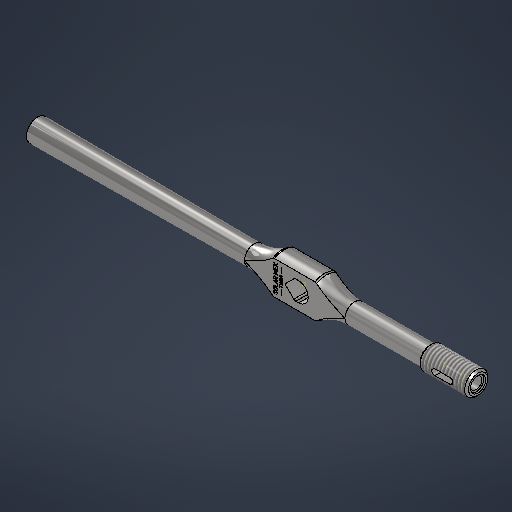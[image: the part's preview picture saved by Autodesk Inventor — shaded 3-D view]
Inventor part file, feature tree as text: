
AUTODESK INVENTOR PART (.ipt)
format: ipt  version: 2025.3 (Build 293356000, 356)  size: 490,496 bytes
history: native  units: mm
features: sketch x5, extrude x2, other x2, fillet x2, revolve x1, thread x1, plane x1, projected_geometry x1
ambient origin geometry x8: Origin, YZ Plane, XZ Plane, XY Plane, X Axis, Y Axis, Z Axis, Center Point
bodies: Solid1 (feature_tree)
feature tree (15):
  sketch  "Sketch1"  dims[d0=7.071068mm d3=2.071068mm]
  revolve  "Revolution1"  [1 undecoded]
  extrude  "Extrusion1"  Depth=52.0mm
  extrude  "Extrusion2"  Depth=1.5mm
  thread  "Thread1"  [1 undecoded]
  other  "Mark2"
  plane  "Work Plane1"
  fillet  "Fillet3"  Radius=6.0mm
  fillet  "Fillet4"  Radius=1.5mm
  sketch  "Sketch5"  dims[d24=1.0mm]
  other  "Work Axis1"
  sketch  "Sketch6"  dims[d25=12.0mm d26=1.0mm d27=1.0mm d28=90.0mm d29=25.0mm d32=360.0deg d33=3.05mm d34=8.0mm d35=0.0mm d36=0.0mm d37=10.0mm d38=0.0mm d39=0.0mm d40=10.0mm d41=11.5mm d42=140.0mm d43=23.0mm d44=0.0mm d46=8.0mm d47=1.0mm d48=50.0mm d49=2.0mm d50=10.0mm d52=10.0mm d54=129.0mm d55=79.0mm d56=1.5mm d57=22.0mm d59=14.930565mm d60=4.048188mm d61=3.0mm d62=1.5mm d63=230.0mm d64=3.0mm]
  sketch  "Sketch2"  dims[d4=0.066855mm d6=52.0mm]
  sketch  "Sketch4"  dims[d7=10.0mm d8=20.0mm d11=5.0mm d17=6.0mm d20=1.5mm d21=1.0mm]
  projected_geometry  "Projected Loop1"
note: 2 required parameter values undecoded (feature->parameter linkage not recoverable at this tier; creation-order binding heuristic only, values carry confidence <= 0.55)